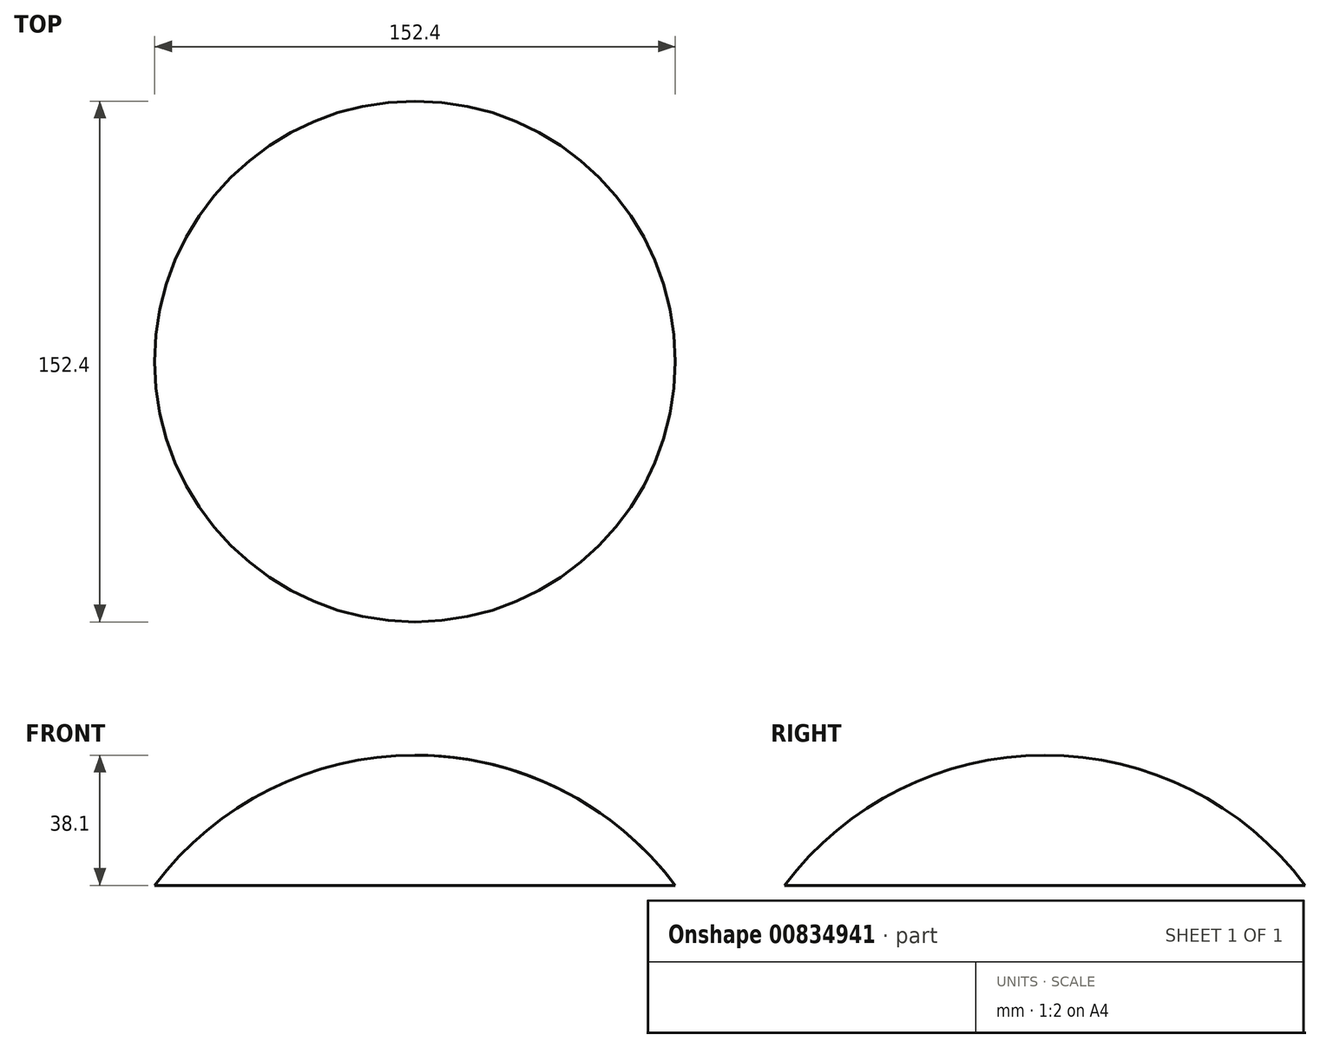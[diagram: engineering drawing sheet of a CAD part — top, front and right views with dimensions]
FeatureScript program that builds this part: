
annotation { "Feature Type Name" : "Feature", "Feature Type Description" : "" }
export const myFeature = defineFeature(function(context is Context, id is Id, definition is map)
    precondition{}
    {
        {
            var Q0;
            Q0=qCreatedBy(makeId("Front.planeOp"),FACE);
            var sketch = newSketch(context, id + "F0", { "sketchPlane" : qUnion([Q0])});
            skArc(sketch, "E0", {"start": v(0, 38.1) * mm, "mid": v(-42.6, 28.04) * mm, "end": v(-76.2, 0) * mm});
            skLineSegment(sketch, "E1", {"start": v(0, 38.1) * mm, "end": v(0, 0) * mm});
            skLineSegment(sketch, "E2", {"start": v(27.15, 38.1) * mm, "end": v(-34.88, 38.1) * mm, "construction": true});
            skLineSegment(sketch, "E3", {"start": v(-76.2, 0) * mm, "end": v(0, 0) * mm});
            skSolve(sketch);
        }
        {
            var Q0;
            Q0 = qSketchRegion(id + "F0", true);
            var Q1;
            Q1=sQuery(id+"F0.wireOp",EDGE,"E1");
            revolve(context, id + "F1", {"surfaceOperationType" : NewSurfaceOperationType.NEW, "entities" : qUnion([Q0]), "axis" : qUnion([Q1]), "revolveType" : RevolveType.FULL});
        }
    });
